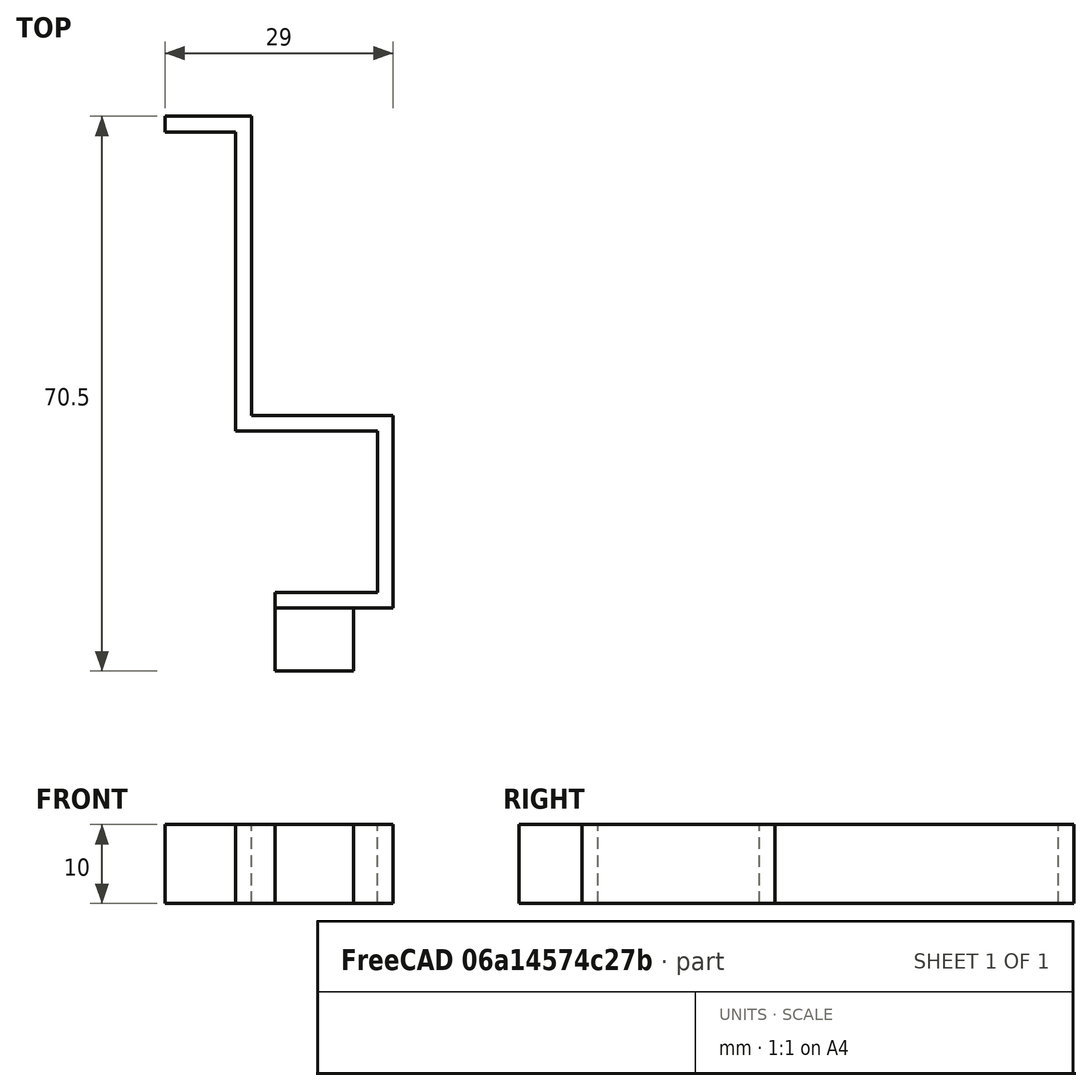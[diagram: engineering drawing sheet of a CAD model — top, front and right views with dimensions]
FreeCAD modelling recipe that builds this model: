
FCSTD DOCUMENT  (FreeCAD 0.18R14555 (Git shallow))
Label: z-grantry-level
License: All rights reserved
LicenseURL: http://en.wikipedia.org/wiki/All_rights_reserved
objects: Part::Feature×2, Sketcher::SketchObject×1, PartDesign::Pad×1, PartDesign::Body×1, Part::Box×1, Part::MultiFuse×1
note: 8 computed .brp shape members not serialized (recipe doc carries the construction recipe); baked Part::Feature solids carry a one-line shape summary decoded from their .brp

FEATURE [Sketcher::SketchObject] Sketch
  MapMode = 5
  Support = -> [XY_Plane]
  sketch-geometry (12):
    g0: LineSegment StartX=0 StartY=0 StartZ=0 EndX=11 EndY=0 EndZ=0
    g1: LineSegment StartX=11 StartY=0 StartZ=0 EndX=11 EndY=-38 EndZ=0
    g2: LineSegment StartX=11 StartY=-38 StartZ=0 EndX=29 EndY=-38 EndZ=0
    g3: LineSegment StartX=29 StartY=-38 StartZ=0 EndX=29 EndY=-62.5 EndZ=0
    g4: LineSegment StartX=29 StartY=-62.5 StartZ=0 EndX=14 EndY=-62.5 EndZ=0
    g5: LineSegment StartX=14 StartY=-62.5 StartZ=0 EndX=14 EndY=-60.5 EndZ=0
    g6: LineSegment StartX=14 StartY=-60.5 StartZ=0 EndX=27 EndY=-60.5 EndZ=0
    g7: LineSegment StartX=27 StartY=-60.5 StartZ=0 EndX=27 EndY=-40 EndZ=0
    g8: LineSegment StartX=27 StartY=-40 StartZ=0 EndX=9 EndY=-40 EndZ=0
    g9: LineSegment StartX=9 StartY=-40 StartZ=0 EndX=9 EndY=-2 EndZ=0
    g10: LineSegment StartX=9 StartY=-2 StartZ=0 EndX=0 EndY=-2 EndZ=0
    g11: LineSegment StartX=0 StartY=-2 StartZ=0 EndX=0 EndY=0 EndZ=0
  constraints (26):
    c: Coincident(g-1,g0)
    c: PointOnObject(g0,g-1)
    c: Coincident(g0,g1)
    c: Vertical(g1)
    c: Coincident(g1,g2)
    c: Horizontal(g2)
    c: Coincident(g2,g3)
    c: Vertical(g3)
    c: Coincident(g3,g4)
    c: Horizontal(g4)
    c: Coincident(g4,g5)
    c: Vertical(g5)
    c: Coincident(g5,g6)
    c: Horizontal(g6)
    c: Coincident(g6,g7)
    c: Vertical(g7)
    c: Coincident(g7,g8)
    c: Horizontal(g8)
    c: Coincident(g8,g9)
    c: Vertical(g9)
    c: Coincident(g9,g10)
    c: PointOnObject(g10,g-2)
    c: Horizontal(g10)
    c: Coincident(g10,g11)
    c: PointOnObject(g11,g0)
    c: Vertical(g11)
FEATURE [PartDesign::Pad] Pad
  Length = 10
  Length2 = 100
  Profile = -> Sketch
  Type = 0
FEATURE [PartDesign::Body] Body
  Group = -> [Sketch,Pad]
  Origin = -> Origin
  Tip = -> Pad
FEATURE [Part::Feature] Body001
  shape: bbox 29 x 62.5 x 10 mm, 14 faces (baked)
FEATURE [Part::Box] Box  label="Cube"
  AttacherType = Attacher::AttachEngine3D
  Height = 10
  Length = 10
  Placement = pos=(14,-70.5,0) rot=(0,0,1;0rad)
  Width = 10
FEATURE [Part::MultiFuse] Fusion
  Shapes = -> [Body001,Box]
FEATURE [Part::Feature] Fusion001
  shape: bbox 29 x 70.5 x 10 mm, 16 faces (baked)
